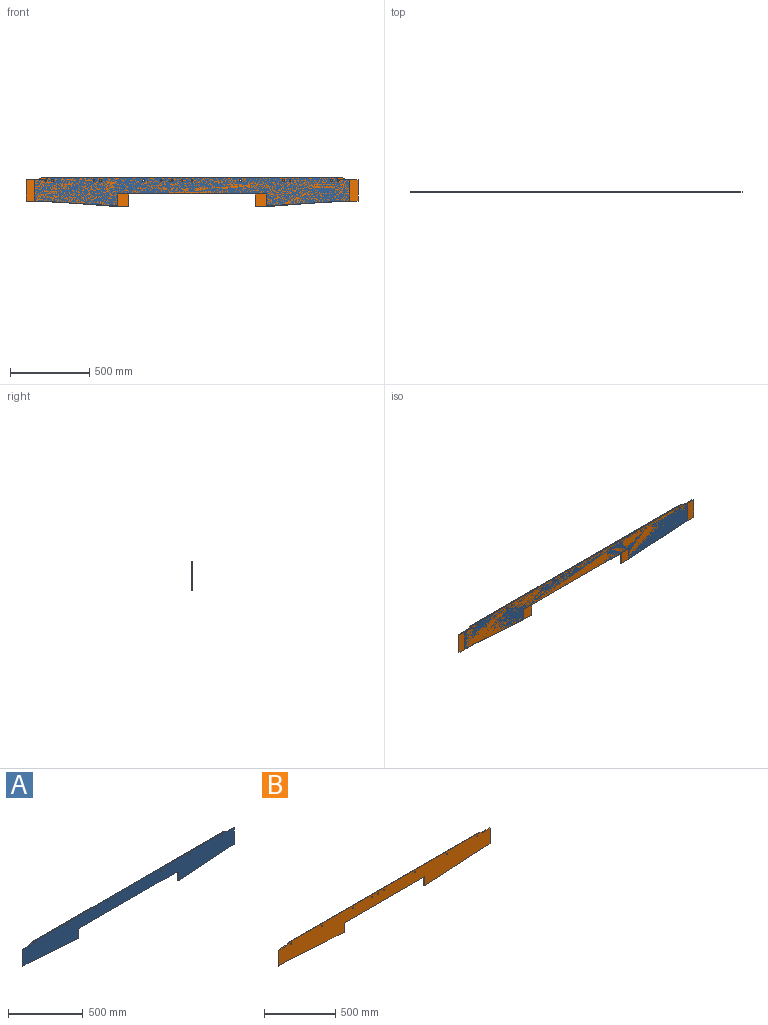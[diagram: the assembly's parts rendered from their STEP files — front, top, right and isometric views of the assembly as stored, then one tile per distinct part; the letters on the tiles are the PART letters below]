
ASSEMBLY  parts=2 mates=1
PART A: 29 faces, bbox 1996x6x185 mm
  f0: plane 1794.2x6mm, normal (0,0,1), area 10765.2mm2, adj f23,f24,f27,f28
  f1: plane 19.44x9.72mm, normal (-0.45,0,0.89), area 130.4mm2, adj f23,f24,f26,f27
  f2: plane 59.1x6mm, normal (0,0,1), area 354.6mm2, adj f3,f23,f24,f26
  f3: plane 135x6mm, normal (-1,0,0), area 810mm2, adj f2,f4,f23,f24
  f4: plane 61x6mm, normal (0,0,-1), area 366mm2, adj f3,f5,f23,f24
  f5: plane 467x35mm, normal (-0.07,0,-1), area 2809.9mm2, adj f4,f6,f23,f24
  f6: plane 80x6mm, normal (1,0,0), area 480mm2, adj f5,f7,f23,f24
  f7: plane 940x6mm, normal (0,0,-1), area 5640mm2, adj f6,f8,f23,f24
  f8: plane 80x6mm, normal (-1,0,0), area 480mm2, adj f7,f9,f23,f24
  f9: plane 467x35mm, normal (0.07,0,-1), area 2809.9mm2, adj f8,f10,f23,f24
  f10: plane 61x6mm, normal (0,0,-1), area 366mm2, adj f9,f11,f23,f24
  f11: plane 135x6mm, normal (1,0,0), area 810mm2, adj f10,f12,f23,f24
  f12: plane 59.1x6mm, normal (0,0,1), area 354.6mm2, adj f11,f23,f24,f25
  f13: cylinder r=5.5mm len=11mm, axis (0,-1,0), area 207.3mm2, adj f23,f24
  f14: cylinder r=5.5mm len=11mm, axis (0,-1,0), area 207.3mm2, adj f23,f24
  f15: cylinder r=5.5mm len=11mm, axis (0,-1,0), area 207.3mm2, adj f23,f24
  f16: cylinder r=5.5mm len=11mm, axis (0,-1,0), area 207.3mm2, adj f23,f24
  f17: cylinder r=5.5mm len=11mm, axis (0,-1,0), area 207.3mm2, adj f23,f24
  f18: cylinder r=5.5mm len=11mm, axis (0,-1,0), area 207.3mm2, adj f23,f24
  f19: cylinder r=5.5mm len=11mm, axis (0,-1,0), area 207.3mm2, adj f23,f24
  f20: cylinder r=5.5mm len=11mm, axis (0,-1,0), area 207.3mm2, adj f23,f24
  f21: cylinder r=5.5mm len=11mm, axis (0,-1,0), area 207.3mm2, adj f23,f24
  f22: plane 19.44x9.72mm, normal (0.45,0,0.89), area 130.4mm2, adj f23,f24,f25,f28
  f23: plane 1996x185mm, normal (0,-1,0), area 270189.7mm2, adj f0,f1,f2,f3,f4,f5,f6,f7
  f24: plane 1996x185mm, normal (0,1,0), area 270189.7mm2, adj f0,f1,f2,f3,f4,f5,f6,f7
  f25: cylinder r=25mm len=11.18mm, axis (0,1,0), area 69.5mm2, adj f12,f22,f23,f24
  f26: cylinder r=25mm len=11.18mm, axis (0,1,0), area 69.5mm2, adj f1,f2,f23,f24
  f27: cylinder r=25mm len=11.18mm, axis (0,1,0), area 69.5mm2, adj f0,f1,f23,f24
  f28: cylinder r=25mm len=11.18mm, axis (0,1,0), area 69.5mm2, adj f0,f22,f23,f24
PART B: 29 faces, bbox 2100x6x185 mm
  f0: plane 1878.2x6mm, normal (0,0,1), area 11269.2mm2, adj f23,f24,f27,f28
  f1: plane 19.44x9.72mm, normal (-0.45,0,0.89), area 130.4mm2, adj f23,f24,f26,f27
  f2: plane 69.1x6mm, normal (0,0,1), area 414.6mm2, adj f3,f23,f24,f26
  f3: plane 135x6mm, normal (-1,0,0), area 810mm2, adj f2,f4,f23,f24
  f4: plane 71x6mm, normal (0,0,-1), area 426mm2, adj f3,f5,f23,f24
  f5: plane 579x35mm, normal (-0.06,0,-1), area 3480.3mm2, adj f4,f6,f23,f24
  f6: plane 80x6mm, normal (1,0,0), area 480mm2, adj f5,f7,f23,f24
  f7: plane 800x6mm, normal (0,0,-1), area 4800mm2, adj f6,f8,f23,f24
  f8: plane 80x6mm, normal (-1,0,0), area 480mm2, adj f7,f9,f23,f24
  f9: plane 579x35mm, normal (0.06,0,-1), area 3480.3mm2, adj f8,f10,f23,f24
  f10: plane 71x6mm, normal (0,0,-1), area 426mm2, adj f9,f11,f23,f24
  f11: plane 135x6mm, normal (1,0,0), area 810mm2, adj f10,f12,f23,f24
  f12: plane 69.1x6mm, normal (0,0,1), area 414.6mm2, adj f11,f23,f24,f25
  f13: cylinder r=5.5mm len=11mm, axis (0,-1,0), area 207.3mm2, adj f23,f24
  f14: cylinder r=5.5mm len=11mm, axis (0,-1,0), area 207.3mm2, adj f23,f24
  f15: cylinder r=5.5mm len=11mm, axis (0,-1,0), area 207.3mm2, adj f23,f24
  f16: cylinder r=5.5mm len=11mm, axis (0,-1,0), area 207.3mm2, adj f23,f24
  f17: cylinder r=5.5mm len=11mm, axis (0,-1,0), area 207.3mm2, adj f23,f24
  f18: cylinder r=5.5mm len=11mm, axis (0,-1,0), area 207.3mm2, adj f23,f24
  f19: cylinder r=5.5mm len=11mm, axis (0,-1,0), area 207.3mm2, adj f23,f24
  f20: cylinder r=5.5mm len=11mm, axis (0,-1,0), area 207.3mm2, adj f23,f24
  f21: cylinder r=5.5mm len=11mm, axis (0,-1,0), area 207.3mm2, adj f23,f24
  f22: plane 19.44x9.72mm, normal (0.45,0,0.89), area 130.4mm2, adj f23,f24,f25,f28
  f23: plane 2100x185mm, normal (0,-1,0), area 295709.7mm2, adj f0,f1,f2,f3,f4,f5,f6,f7
  f24: plane 2100x185mm, normal (0,1,0), area 295709.7mm2, adj f0,f1,f2,f3,f4,f5,f6,f7
  f25: cylinder r=25mm len=11.18mm, axis (0,1,0), area 69.5mm2, adj f12,f22,f23,f24
  f26: cylinder r=25mm len=11.18mm, axis (0,1,0), area 69.5mm2, adj f1,f2,f23,f24
  f27: cylinder r=25mm len=11.18mm, axis (0,1,0), area 69.5mm2, adj f0,f1,f23,f24
  f28: cylinder r=25mm len=11.18mm, axis (0,1,0), area 69.5mm2, adj f0,f22,f23,f24
PLACE A t=(64.75,-152.33,-36.61)mm
PLACE B t=(22.75,-152.33,-36.61)mm
MATE fastened B.f17 <-> A.f17  axis (0,-1,0) through (757.25,-158.33,128.39)mm
